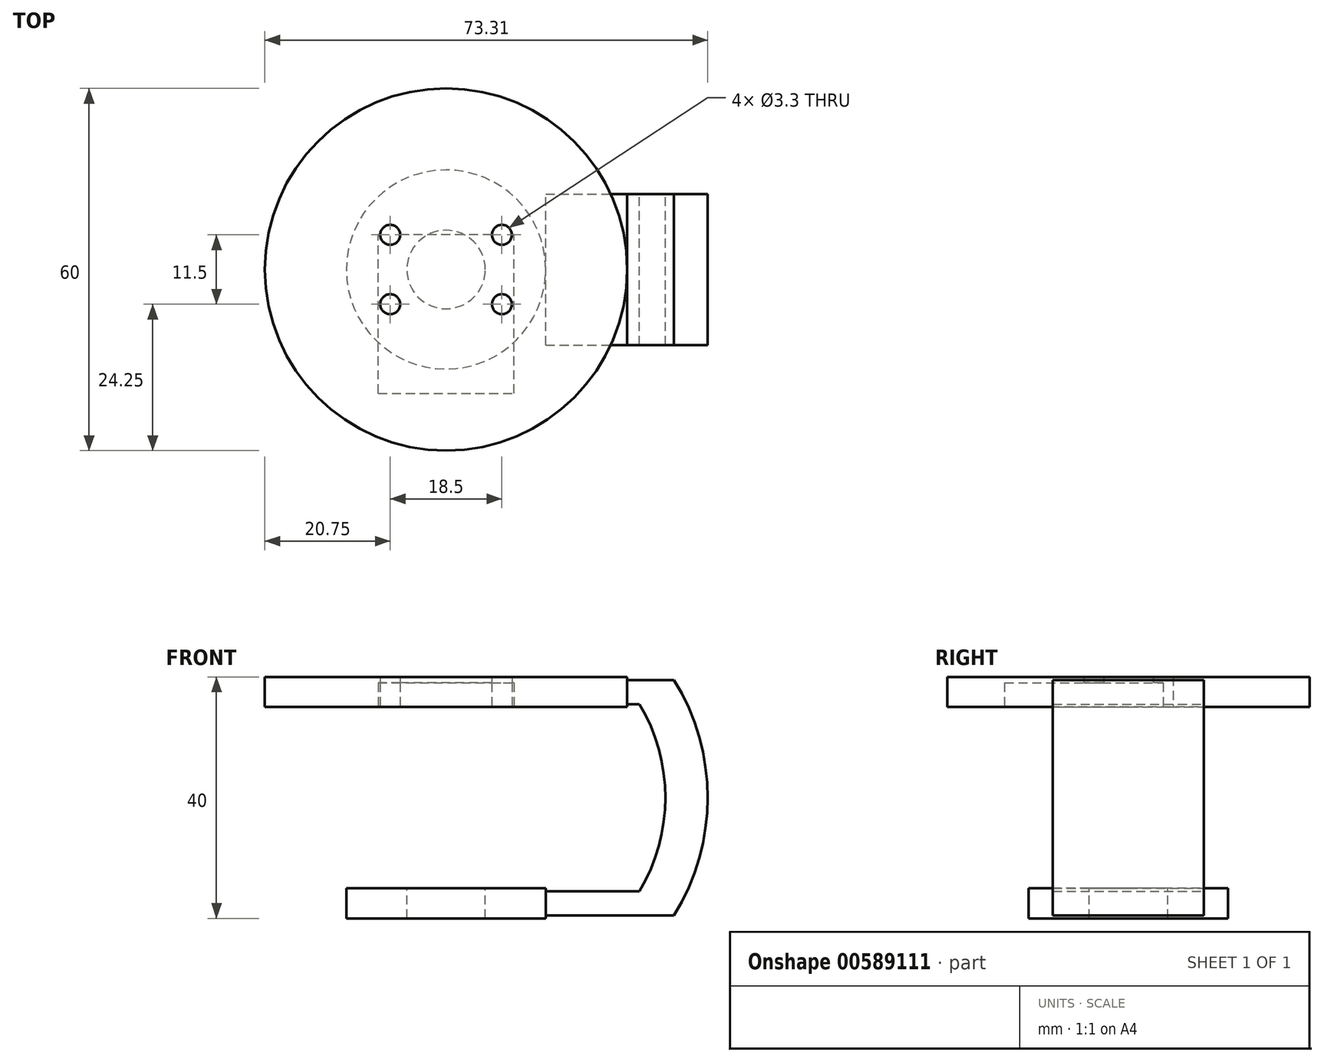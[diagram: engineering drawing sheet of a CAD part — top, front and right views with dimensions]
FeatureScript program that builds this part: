
annotation { "Feature Type Name" : "Feature", "Feature Type Description" : "" }
export const myFeature = defineFeature(function(context is Context, id is Id, definition is map)
    precondition{}
    {
        {
            var Q0;
            Q0=qCreatedBy(makeId("Front.planeOp"),FACE);
            var sketch = newSketch(context, id + "F0", { "sketchPlane" : qUnion([Q0])});
            skLineSegment(sketch, "E0.bottom", {"start": v(16.5, 2.5) * mm, "end": v(-16.5, 2.5) * mm});
            skLineSegment(sketch, "E0.top", {"start": v(16.5, -2.5) * mm, "end": v(-16.5, -2.5) * mm});
            skLineSegment(sketch, "E0.left", {"start": v(16.5, 2.5) * mm, "end": v(16.5, -2.5) * mm});
            skLineSegment(sketch, "E0.right", {"start": v(-16.5, 2.5) * mm, "end": v(-16.5, -2.5) * mm});
            skPoint(sketch, "E0.middle", {"position": v(0, 0) * mm});
            skLineSegment(sketch, "E1", {"start": v(0, 2.5) * mm, "end": v(0, -2.5) * mm});
            skLineSegment(sketch, "E2.bottom", {"start": v(0, -2) * mm, "end": v(32, -2) * mm});
            skLineSegment(sketch, "E2.top", {"start": v(0, 2) * mm, "end": v(32, 2) * mm});
            skLineSegment(sketch, "E2.left", {"start": v(0, -2) * mm, "end": v(0, 2) * mm});
            skLineSegment(sketch, "E2.right", {"start": v(32, -2) * mm, "end": v(32, 2) * mm});
            skLineSegment(sketch, "E3.bottom", {"start": v(30, 37.5) * mm, "end": v(-30, 37.5) * mm});
            skLineSegment(sketch, "E3.top", {"start": v(30, 32.5) * mm, "end": v(-30, 32.5) * mm});
            skLineSegment(sketch, "E3.left", {"start": v(30, 37.5) * mm, "end": v(30, 32.5) * mm});
            skLineSegment(sketch, "E3.right", {"start": v(-30, 37.5) * mm, "end": v(-30, 32.5) * mm});
            skPoint(sketch, "E3.middle", {"position": v(0, 35) * mm});
            skLineSegment(sketch, "E4", {"start": v(0, 37.5) * mm, "end": v(0, 32.5) * mm});
            skLineSegment(sketch, "E5.bottom", {"start": v(0, 33) * mm, "end": v(32, 33) * mm});
            skLineSegment(sketch, "E5.top", {"start": v(0, 37) * mm, "end": v(32, 37) * mm});
            skLineSegment(sketch, "E5.left", {"start": v(0, 33) * mm, "end": v(0, 37) * mm});
            skLineSegment(sketch, "E5.right", {"start": v(32, 33) * mm, "end": v(32, 37) * mm});
            skArc(sketch, "E6", {"start": v(32, 2) * mm, "mid": v(36.31, 17.5) * mm, "end": v(32, 33) * mm});
            skArc(sketch, "E7.0", {"start": v(37.76, -2) * mm, "mid": v(43.31, 17.5) * mm, "end": v(37.76, 37) * mm});
            skLineSegment(sketch, "E8", {"start": v(32, 37) * mm, "end": v(37.76, 37) * mm});
            skLineSegment(sketch, "E9", {"start": v(32, -2) * mm, "end": v(37.76, -2) * mm});
            skSolve(sketch);
        }
        {
            var Q0;
            {var subQ0=sQuery(id+"F0.wireOp",EDGE,"E0.right");Q0=makeQuery(id+"F0.imprint","IMPRINT",FACE,{"disambiguationData":[TD([[makeQuery(id+"F0.imprint","IMPRINT",EDGE,{"derivedFrom":subQ0}),1.0]])]});}
            var Q1;
            Q1=sQuery(id+"F0.wireOp",EDGE,"E1");
            revolve(context, id + "F1", {"entities" : qUnion([Q0]), "axis" : qUnion([Q1]), "revolveType" : RevolveType.FULL});
        }
        {
            var Q0;
            {var subQ0=sQuery(id+"F0.wireOp",EDGE,"E3.right");Q0=makeQuery(id+"F0.imprint","IMPRINT",FACE,{"disambiguationData":[TD([[makeQuery(id+"F0.imprint","IMPRINT",EDGE,{"derivedFrom":subQ0}),1.0]])]});}
            var Q1;
            Q1=sQuery(id+"F0.wireOp",EDGE,"E4");
            revolve(context, id + "F2", {"entities" : qUnion([Q0]), "axis" : qUnion([Q1]), "revolveType" : RevolveType.FULL});
        }
        {
            var Q0;
            {var subQ5=sQuery(id+"F0.wireOp",EDGE,"E2.right");Q0=makeQuery(id+"F0.imprint","IMPRINT",FACE,{"disambiguationData":[TD([[makeQuery(id+"F0.imprint","IMPRINT",EDGE,{"derivedFrom":subQ5}),1.0]])]});}
            var Q1;
            Q1=makeQuery(id+"F0.imprint","IMPRINT",FACE,{"disambiguationData":[TD([[makeQuery(id+"F0.imprint","IMPRINT",EDGE,{"derivedFrom":sQuery(id+"F0.wireOp",EDGE,"E2.right")}),-1.0]])]});
            var Q2;
            {var subQ5=sQuery(id+"F0.wireOp",EDGE,"E5.right");Q2=makeQuery(id+"F0.imprint","IMPRINT",FACE,{"disambiguationData":[TD([[makeQuery(id+"F0.imprint","IMPRINT",EDGE,{"derivedFrom":subQ5}),1.0]])]});}
            var Q3;
            {var subQ5=sQuery(id+"F0.wireOp",EDGE,"E2.left");Q3=makeQuery(id+"F0.imprint","IMPRINT",FACE,{"disambiguationData":[TD([[makeQuery(id+"F0.imprint","IMPRINT",EDGE,{"derivedFrom":subQ5}),-1.0]])]});}
            var Q4;
            {var subQ5=sQuery(id+"F0.wireOp",EDGE,"E5.left");Q4=makeQuery(id+"F0.imprint","IMPRINT",FACE,{"disambiguationData":[TD([[makeQuery(id+"F0.imprint","IMPRINT",EDGE,{"derivedFrom":subQ5}),-1.0]])]});}
            extrude(context, id + "F3", {"entities" : qUnion([Q0, Q1, Q2, Q3, Q4]), "endBound" : BoundingType.SYMMETRIC, "depth" : 25 * mm, "offsetDistance" : 25 * mm});
        }
        {
            var Q0;
            Q0=makeQuery(id+"F1.opRevolve","SWEPT_FACE",FACE,{"disambiguationData":[OSD([sQuery(id+"F0.wireOp",EDGE,"E0.bottom")])]});
            var sketch = newSketch(context, id + "F4", { "sketchPlane" : qUnion([Q0])});
            skCircle(sketch, "E10", {"center": v(0, 0) * mm, "radius": 12 * mm});
            skPoint(sketch, "E11", {"position": v(0, 12) * mm});
            skSolve(sketch);
        }
        {
            var Q0;
            Q0=sQuery(id+"F4.wireOp",VERTEX,"E11");
            var Q1;
            Q1=makeQuery(id+"F2.opRevolve","SWEPT_BODY",BODY,{"disambiguationData":[OSD([sQuery(id+"F0.wireOp",EDGE,"E3.bottom"),sQuery(id+"F0.wireOp",EDGE,"E3.top"),sQuery(id+"F0.wireOp",EDGE,"E3.right"),sQuery(id+"F0.wireOp",EDGE,"E4"),sQuery(id+"F0.wireOp",EDGE,"E5.left")])]});
            hole(context, id + "F5", {"style" : HoleStyle.SIMPLE, "endStyle" : HoleEndStyle.THROUGH, "standardTappedOrClearance" : lookupTablePath({ "standard" : "ISO", "fit" : "Normal", "size" : "M3", "type" : "Clearance" }), "standardBlindInLast" : lookupTablePath({ "fit" : "Standard", "standard" : "ISO", "size" : "M3", "type" : "Clearance" }), "holeDiameter" : 3.3 * mm, "isTappedThrough" : true, "tappedDepth" : 12.7 * mm, "tapClearance" : 3, "locations" : qUnion([Q0]), "scope" : qUnion([Q1])});
        }
        {
            var Q0;
            Q0=makeQuery(id+"F1.opRevolve","SWEPT_FACE",FACE,{"disambiguationData":[OSD([sQuery(id+"F0.wireOp",EDGE,"E0.bottom")])]});
            var sketch = newSketch(context, id + "F6", { "sketchPlane" : qUnion([Q0])});
            skCircle(sketch, "E12", {"center": v(0, 0) * mm, "radius": 6.5 * mm});
            skSolve(sketch);
        }
        {
            var Q0;
            Q0=makeQuery(id+"F6.imprint","IMPRINT",FACE,{"disambiguationData":[TD([[makeQuery(id+"F6.imprint","IMPRINT",EDGE,{"derivedFrom":sQuery(id+"F6.wireOp",EDGE,"E12")}),1.0]])]});
            extrude(context, id + "F7", {"entities" : qUnion([Q0]), "operationType" : NewBodyOperationType.REMOVE, "oppositeDirection" : true, "depth" : 6 * mm, "offsetDistance" : 25 * mm});
        }
        {
            var Q0;
            Q0=makeQuery(id+"F2.opRevolve","SWEPT_FACE",FACE,{"disambiguationData":[OSD([sQuery(id+"F0.wireOp",EDGE,"E3.top")])]});
            var sketch = newSketch(context, id + "F8", { "sketchPlane" : qUnion([Q0])});
            skLineSegment(sketch, "E13.bottom", {"start": v(11.25, 5.75) * mm, "end": v(-11.25, 5.75) * mm});
            skLineSegment(sketch, "E13.top", {"start": v(11.25, -5.75) * mm, "end": v(-11.25, -5.75) * mm});
            skLineSegment(sketch, "E13.left", {"start": v(11.25, 5.75) * mm, "end": v(11.25, -5.75) * mm});
            skLineSegment(sketch, "E13.right", {"start": v(-11.25, 5.75) * mm, "end": v(-11.25, -5.75) * mm});
            skPoint(sketch, "E13.middle", {"position": v(0, 0) * mm});
            skLineSegment(sketch, "E14.bottom", {"start": v(-11.25, -5.75) * mm, "end": v(10.8, -5.75) * mm});
            skLineSegment(sketch, "E14.top", {"start": v(-11.25, 20.5) * mm, "end": v(11.25, 20.5) * mm});
            skLineSegment(sketch, "E14.left", {"start": v(-11.25, -8) * mm, "end": v(-11.25, 20.5) * mm});
            skLineSegment(sketch, "E14.right", {"start": v(11.25, -8) * mm, "end": v(11.25, 20.5) * mm});
            skLineSegment(sketch, "E15", {"start": v(-11.25, -8) * mm, "end": v(11.25, -8) * mm});
            skPoint(sketch, "E16", {"position": v(-9.25, -5.75) * mm});
            skPoint(sketch, "E17", {"position": v(9.25, -5.75) * mm});
            skPoint(sketch, "E18", {"position": v(9.25, 5.75) * mm});
            skPoint(sketch, "E19", {"position": v(-9.25, 5.75) * mm});
            skSolve(sketch);
        }
        {
            var Q0;
            Q0=sQuery(id+"F8.wireOp",VERTEX,"E16");
            var Q1;
            Q1=sQuery(id+"F8.wireOp",VERTEX,"E19");
            var Q2;
            Q2=sQuery(id+"F8.wireOp",VERTEX,"E18");
            var Q3;
            Q3=sQuery(id+"F8.wireOp",VERTEX,"E17");
            var Q4;
            Q4=makeQuery(id+"F2.opRevolve","SWEPT_BODY",BODY,{"disambiguationData":[OSD([sQuery(id+"F0.wireOp",EDGE,"E3.bottom"),sQuery(id+"F0.wireOp",EDGE,"E3.top"),sQuery(id+"F0.wireOp",EDGE,"E3.right"),sQuery(id+"F0.wireOp",EDGE,"E4"),sQuery(id+"F0.wireOp",EDGE,"E5.left")])]});
            hole(context, id + "F9", {"style" : HoleStyle.SIMPLE, "endStyle" : HoleEndStyle.THROUGH, "standardTappedOrClearance" : lookupTablePath({ "standard" : "ISO", "fit" : "Normal", "size" : "M3", "type" : "Clearance" }), "standardBlindInLast" : lookupTablePath({ "fit" : "Standard", "standard" : "ISO", "size" : "M3", "type" : "Clearance" }), "holeDiameter" : 3.3 * mm, "isTappedThrough" : true, "tappedDepth" : 12.7 * mm, "tapClearance" : 3, "locations" : qUnion([Q0, Q1, Q2, Q3]), "scope" : qUnion([Q4]), "majorDiameter" : 5 * mm});
        }
        {
            var Q0;
            {var subQ0=sQuery(id+"F8.wireOp",EDGE,"E14.bottom");Q0=makeQuery(id+"F8.imprint","IMPRINT",FACE,{"disambiguationData":[TD([[makeQuery(id+"F8.imprint","IMPRINT",EDGE,{"derivedFrom":subQ0}),-1.0]])]});}
            var Q1;
            {var subQ0=sQuery(id+"F8.wireOp",EDGE,"E13.bottom");Q1=makeQuery(id+"F8.imprint","IMPRINT",FACE,{"disambiguationData":[TD([[makeQuery(id+"F8.imprint","IMPRINT",EDGE,{"derivedFrom":subQ0}),1.0]])]});}
            var Q2;
            {var subQ0=sQuery(id+"F8.wireOp",EDGE,"E13.bottom");Q2=makeQuery(id+"F8.imprint","IMPRINT",FACE,{"disambiguationData":[TD([[makeQuery(id+"F8.imprint","IMPRINT",EDGE,{"derivedFrom":subQ0}),-1.0]])]});}
            extrude(context, id + "F10", {"entities" : qUnion([Q0, Q1, Q2]), "operationType" : NewBodyOperationType.REMOVE, "oppositeDirection" : true, "depth" : 4 * mm, "offsetDistance" : 25 * mm});
        }
    });
